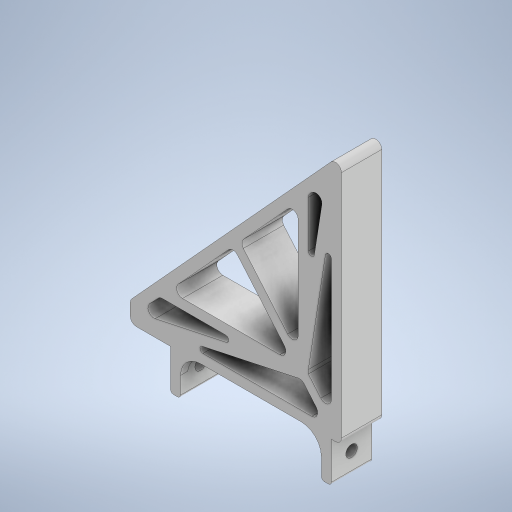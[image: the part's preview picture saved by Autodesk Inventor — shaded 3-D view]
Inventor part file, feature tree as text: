
AUTODESK INVENTOR PART (.ipt)
format: ipt  version: 2024.1 (Build 281209000, 209)  size: 412,160 bytes
history: native  units: mm
features: sketch x7, extrude x5, fillet x4, hole x2
ambient origin geometry x8: Origin, YZ Plane, XZ Plane, XY Plane, X Axis, Y Axis, Z Axis, Center Point
bodies: Solid1 (feature_tree)
feature tree (18):
  extrude  "Extrusion1"  Depth=10.0mm
  extrude  "Extrusion2"  Depth=5.0mm
  fillet  "Fillet1"  Radius=20.0mm
  fillet  "Fillet2"  Radius=2.5mm
  extrude  "Extrusion3"  Depth=5.0mm
  fillet  "Fillet3"  Radius=5.0mm
  fillet  "Fillet4"  Radius=20.0mm
  hole  "Hole2"  [1 undecoded]
  extrude  "Extrusion4"  Depth=5.0mm
  hole  "Hole3"  [1 undecoded]
  extrude  "Extrusion5"  Depth=10.0mm
  sketch  "Sketch1"  dims[d0=10.0mm d1=105.0mm]
  sketch  "Sketch2"  dims[d2=125.0mm d3=5.0mm d4=20.0mm d5=0.0mm d8=2.5mm]
  sketch  "Sketch5"  dims[d9=2.5mm d10=5.0mm d11=5.0mm d12=20.0mm d13=0.0mm]
  sketch  "Sketch6"  dims[d14=3.0mm d16=5.0mm]
  sketch  "Sketch7"  dims[d17=2.094395mm d18=5.0mm]
  sketch  "Sketch8"  dims[d19=1.570796mm d20=1.5mm]
  sketch  "Sketch9"  dims[d35=5.0mm d36=20.0mm d37=80.0mm d38=5.0mm d39=20.0mm d40=0.0mm d41=1.5mm d42=10.0mm d43=5.8mm d44=6.0mm d45=10.4mm d46=2.0mm d47=90.0deg d48=8.0mm d49=0.0mm d50=10.0mm d51=10.0mm d52=20.0mm d53=3.5mm d54=10.0mm d55=0.0mm d56=5.8mm d57=6.0mm d58=4.0mm d59=2.0mm d60=90.0deg d61=8.0mm d62=0.0mm d63=10.0mm d64=10.0mm d65=10.0mm d66=0.0mm]
note: 2 required parameter values undecoded (feature->parameter linkage not recoverable at this tier; creation-order binding heuristic only, values carry confidence <= 0.55)
